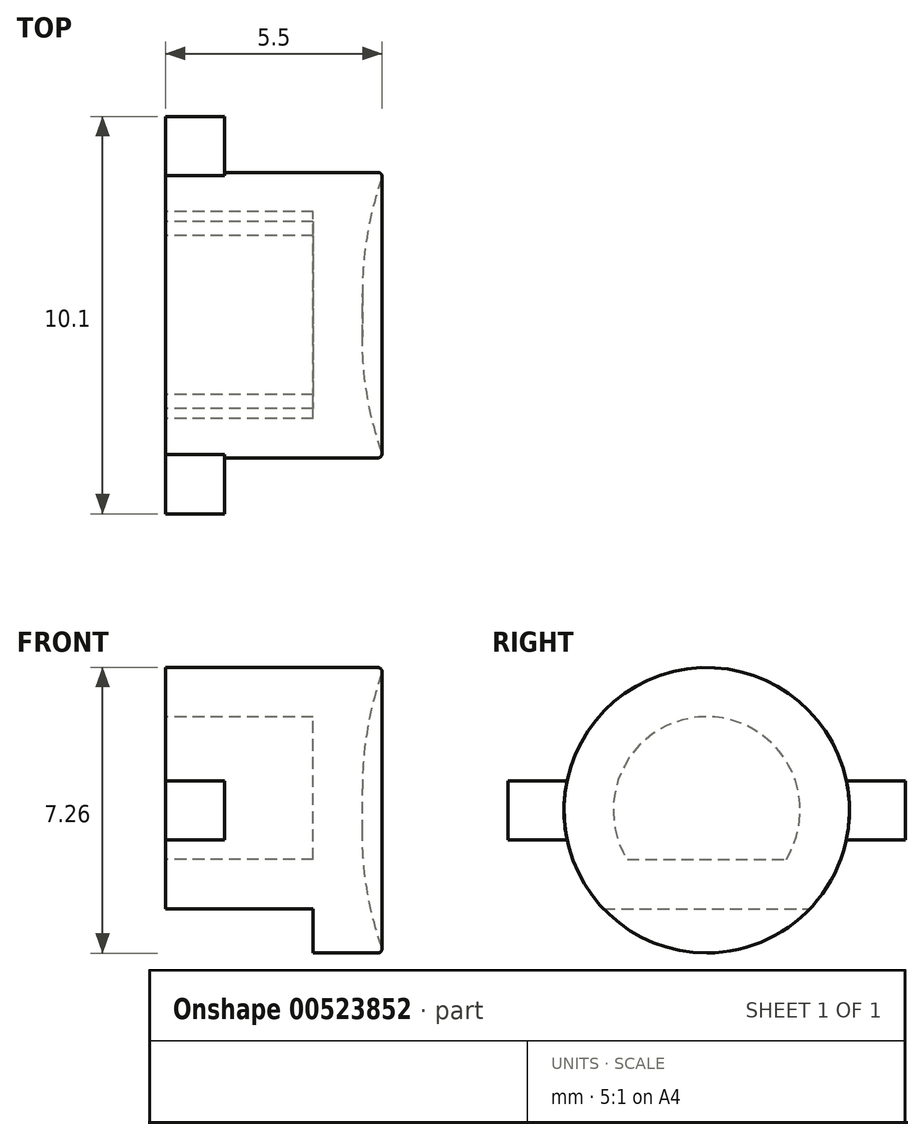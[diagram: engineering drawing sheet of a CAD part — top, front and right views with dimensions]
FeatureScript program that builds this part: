
annotation { "Feature Type Name" : "Feature", "Feature Type Description" : "" }
export const myFeature = defineFeature(function(context is Context, id is Id, definition is map)
    precondition{}
    {
        {
            var Q0;
            Q0=qCreatedBy(makeId("Right.planeOp"),FACE);
            var sketch = newSketch(context, id + "F0", { "sketchPlane" : qUnion([Q0])});
            skCircle(sketch, "E0", {"center": v(0, 0) * mm, "radius": 3.62 * mm});
            skSolve(sketch);
        }
        {
            var Q0;
            Q0=makeQuery(id+"F0.imprint","IMPRINT",FACE,{"disambiguationData":[TD([[makeQuery(id+"F0.imprint","IMPRINT",EDGE,{"derivedFrom":sQuery(id+"F0.wireOp",EDGE,"E0")}),1.0]])]});
            extrude(context, id + "F1", {"entities" : qUnion([Q0]), "endBound" : BoundingType.SYMMETRIC, "depth" : 5.5 * mm, "offsetDistance" : 25 * mm});
        }
        {
            var Q0;
            Q0=makeQuery(id+"F1.opExtrude","CAP_FACE",FACE,{"disambiguationData":[OSD([sQuery(id+"F0.wireOp",EDGE,"E0")])],"isStart":true});
            var sketch = newSketch(context, id + "F2", { "sketchPlane" : qUnion([Q0])});
            skLineSegment(sketch, "E1.left", {"start": v(5.05, -0.75) * mm, "end": v(5.05, 0.75) * mm});
            skLineSegment(sketch, "E2.left", {"start": v(-5.05, 0.75) * mm, "end": v(-5.05, -0.75) * mm});
            skLineSegment(sketch, "E3", {"start": v(5.05, 0.75) * mm, "end": v(3.55, 0.75) * mm});
            skLineSegment(sketch, "E4", {"start": v(5.05, -0.75) * mm, "end": v(3.55, -0.75) * mm});
            skArc(sketch, "E5", {"start": v(-3.55, 0.75) * mm, "mid": v(-3.63, 0) * mm, "end": v(-3.55, -0.75) * mm});
            skLineSegment(sketch, "E6", {"start": v(-5.05, 0.75) * mm, "end": v(-3.55, 0.75) * mm});
            skLineSegment(sketch, "E7", {"start": v(-5.05, -0.75) * mm, "end": v(-3.55, -0.75) * mm});
            skArc(sketch, "E8.trimOffspring", {"start": v(3.55, -0.75) * mm, "mid": v(3.63, 0) * mm, "end": v(3.55, 0.75) * mm});
            skPoint(sketch, "E9", {"position": v(5.05, 0) * mm});
            skPoint(sketch, "E10", {"position": v(-5.05, 0) * mm});
            skSolve(sketch);
        }
        {
            var Q0;
            Q0=qSketchRegion(id+"F2",true);
            extrude(context, id + "F3", {"entities" : qUnion([Q0]), "operationType" : NewBodyOperationType.ADD, "oppositeDirection" : true, "depth" : 1.5 * mm, "offsetDistance" : 25 * mm});
        }
        {
            var Q0;
            Q0=makeQuery(id+"F1.opExtrude","CAP_FACE",FACE,{"disambiguationData":[OSD([sQuery(id+"F0.wireOp",EDGE,"E0")])],"isStart":false});
            var sketch = newSketch(context, id + "F4", { "sketchPlane" : qUnion([Q0])});
            skCircle(sketch, "E11", {"center": v(0, 0) * mm, "radius": 3.5 * mm});
            skSolve(sketch);
        }
        {
            var Q0;
            Q0=qSketchRegion(id+"F4",true);
            extrude(context, id + "F5", {"entities" : qUnion([Q0]), "operationType" : NewBodyOperationType.REMOVE, "oppositeDirection" : true, "depth" : .5 * mm, "offsetDistance" : 25 * mm});
        }
        {
            var Q0;
            Q0=makeQuery(id+"F3.boolean.opBoolean","MERGE",FACE,{"derivedFrom":[makeQuery(id+"F1.opExtrude","CAP_FACE",FACE,{"disambiguationData":[OSD([sQuery(id+"F0.wireOp",EDGE,"E0")])],"isStart":true}),makeQuery(id+"F3.opExtrude","CAP_FACE",FACE,{"disambiguationData":[OSD([sQuery(id+"F2.wireOp",EDGE,"E1.left"),sQuery(id+"F2.wireOp",EDGE,"E3"),sQuery(id+"F2.wireOp",EDGE,"E4"),sQuery(id+"F2.wireOp",EDGE,"E8.trimOffspring")])],"isStart":true}),makeQuery(id+"F3.opExtrude","CAP_FACE",FACE,{"disambiguationData":[OSD([sQuery(id+"F2.wireOp",EDGE,"E2.left"),sQuery(id+"F2.wireOp",EDGE,"E5"),sQuery(id+"F2.wireOp",EDGE,"E6"),sQuery(id+"F2.wireOp",EDGE,"E7")])],"isStart":true})]});
            var sketch = newSketch(context, id + "F6", { "sketchPlane" : qUnion([Q0])});
            skArc(sketch, "E12", {"start": v(-2.62, -2.5) * mm, "mid": v(0, -3.63) * mm, "end": v(2.63, -2.5) * mm});
            skLineSegment(sketch, "E13", {"start": v(2.63, -2.5) * mm, "end": v(-2.62, -2.5) * mm});
            skSolve(sketch);
        }
        {
            var Q0;
            Q0 = qSketchRegion(id + "F6", true);
            extrude(context, id + "F7", {"entities" : qUnion([Q0]), "operationType" : NewBodyOperationType.REMOVE, "oppositeDirection" : true, "depth" : 3.75 * mm, "offsetDistance" : 25 * mm});
        }
        {
            var Q0;
            Q0=makeQuery(id+"F1.opExtrude","CAP_FACE",FACE,{"disambiguationData":[OSD([sQuery(id+"F0.wireOp",EDGE,"E0")])],"isStart":true});
            shell(context, id + "F8", {"entities" : qUnion([Q0]), "thickness" : 1.25 * mm});
        }
        {
            var Q0;
            Q0=makeQuery(id+"F5.boolean.opBoolean","COPY",FACE,{"derivedFrom":makeQuery(id+"F5.opExtrude","CAP_FACE",FACE,{"disambiguationData":[OSD([sQuery(id+"F4.wireOp",EDGE,"E11")])],"isStart":false})});
            fillet(context, id + "F9", {"entities" : qUnion([Q0]), "radius" : 9 * mm, "tangentPropagation" : true, "allowEdgeOverflow" : false});
        }
        {
            var Q0;
            Q0=makeQuery(id+"F9.opFillet","BLEND_EDGE",EDGE,{"blendedFrom":[makeQuery(id+"F5.boolean.opBoolean","COPY",EDGE,{"derivedFrom":makeQuery(id+"F5.opExtrude","CAP_EDGE",EDGE,{"disambiguationData":[OSD([sQuery(id+"F4.wireOp",EDGE,"E11")])],"isStart":false})}),makeQuery(id+"F1.opExtrude","CAP_FACE",FACE,{"disambiguationData":[OSD([sQuery(id+"F0.wireOp",EDGE,"E0")])],"isStart":false})],"blendedInto":[makeQuery(id+"F1.opExtrude","CAP_FACE",FACE,{"disambiguationData":[OSD([sQuery(id+"F0.wireOp",EDGE,"E0")])],"isStart":false})]});
            var Q1;
            Q1=makeQuery(id+"F1.opExtrude","CAP_EDGE",EDGE,{"disambiguationData":[OSD([sQuery(id+"F0.wireOp",EDGE,"E0")])],"isStart":false});
            fillet(context, id + "F10", {"entities" : qUnion([Q0, Q1]), "radius" : .1 * mm, "tangentPropagation" : true, "allowEdgeOverflow" : false});
        }
    });
